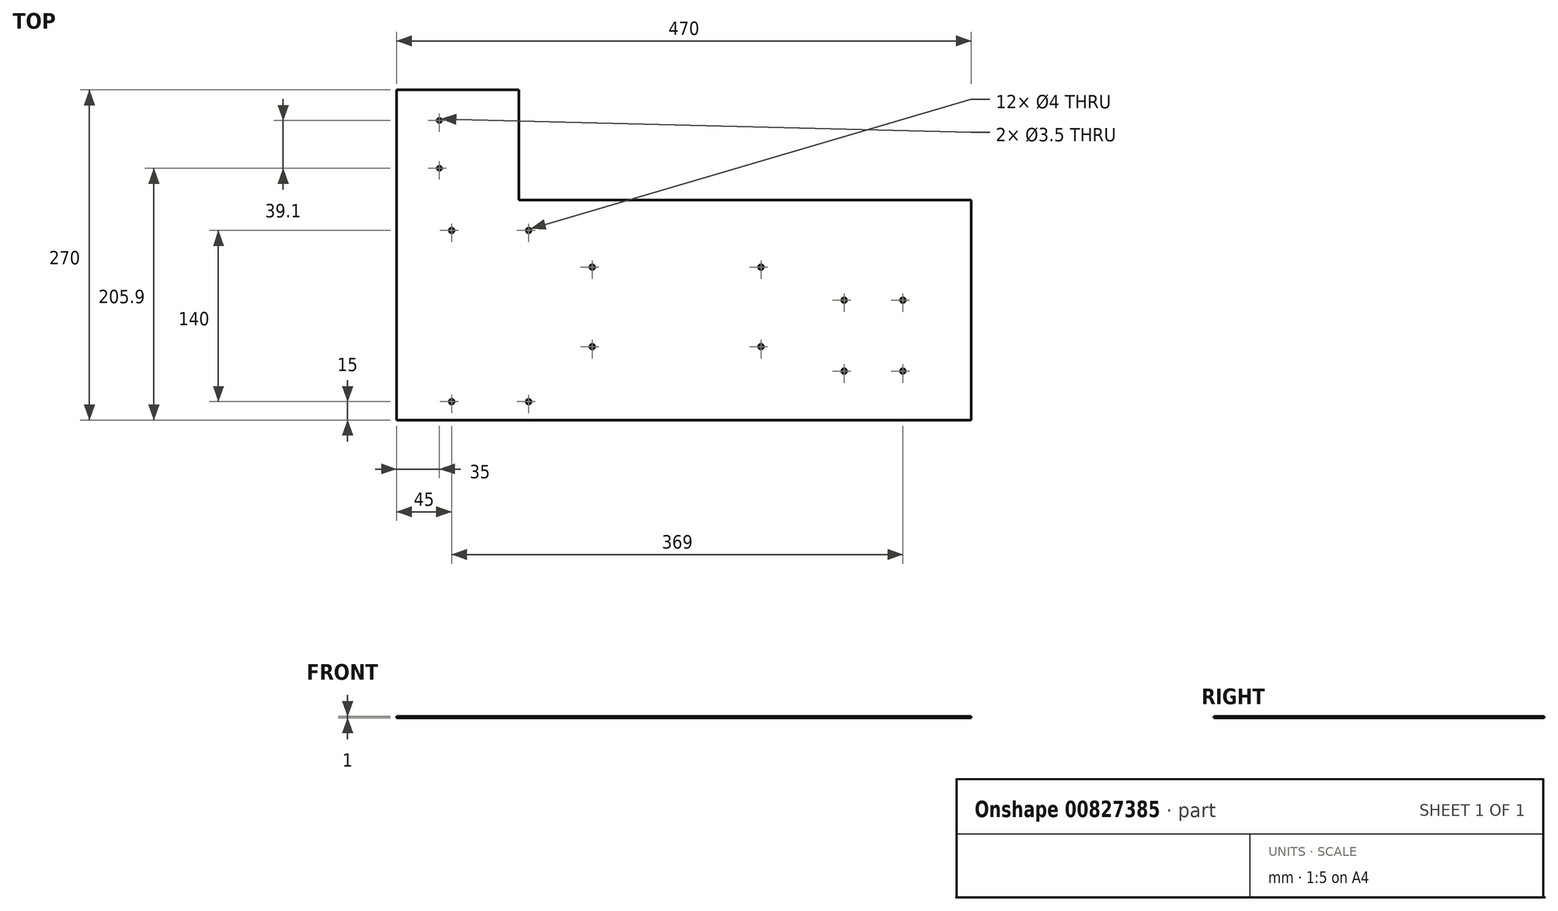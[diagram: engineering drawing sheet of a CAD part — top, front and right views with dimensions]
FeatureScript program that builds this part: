
annotation { "Feature Type Name" : "Feature", "Feature Type Description" : "" }
export const myFeature = defineFeature(function(context is Context, id is Id, definition is map)
    precondition{}
    {
        {
            var Q0;
            Q0=qCreatedBy(makeId("Top.planeOp"),FACE);
            var sketch = newSketch(context, id + "F0", { "sketchPlane" : qUnion([Q0])});
            skLineSegment(sketch, "E0.bottom", {"start": v(-235, 90) * mm, "end": v(-135, 90) * mm, "construction": true});
            skLineSegment(sketch, "E0.top", {"start": v(-235, -90) * mm, "end": v(235, -90) * mm});
            skLineSegment(sketch, "E0.left", {"start": v(-235, 90) * mm, "end": v(-235, -90) * mm});
            skLineSegment(sketch, "E0.right", {"start": v(235, 90) * mm, "end": v(235, -90) * mm});
            skPoint(sketch, "E0.middle", {"position": v(0, 0) * mm});
            skLineSegment(sketch, "E1", {"start": v(-135, 90) * mm, "end": v(-135, 180) * mm});
            skLineSegment(sketch, "E2", {"start": v(-135, 180) * mm, "end": v(-235, 180) * mm});
            skLineSegment(sketch, "E3", {"start": v(-235, 180) * mm, "end": v(-235, 90) * mm});
            skLineSegment(sketch, "E4", {"start": v(-135, 90) * mm, "end": v(235, 90) * mm});
            skSolve(sketch);
        }
        {
            var Q0;
            Q0 = qSketchRegion(id + "F0", true);
            extrude(context, id + "F1", {"entities" : qUnion([Q0]), "depth" : 1 * mm, "offsetDistance" : 25 * mm});
        }
        {
            var Q0;
            Q0=makeQuery(id+"F1.opExtrude","CAP_FACE",FACE,{"disambiguationData":[OSD([sQuery(id+"F0.wireOp",EDGE,"E0.bottom"),sQuery(id+"F0.wireOp",EDGE,"E0.top"),sQuery(id+"F0.wireOp",EDGE,"E0.left"),sQuery(id+"F0.wireOp",EDGE,"E0.right")])],"isStart":false});
            var sketch = newSketch(context, id + "F2", { "sketchPlane" : qUnion([Q0])});
            skLineSegment(sketch, "E5", {"start": v(-419.49, -5) * mm, "end": v(102.49, -5) * mm, "construction": true});
            skLineSegment(sketch, "E6", {"start": v(-158.5, -99.39) * mm, "end": v(-158.5, -5) * mm, "construction": true});
            skPoint(sketch, "E7", {"position": v(-190, 65) * mm});
            skPoint(sketch, "E8.MirrorP", {"position": v(-127, 65) * mm});
            skPoint(sketch, "E9.MirrorP", {"position": v(-127, -75) * mm});
            skPoint(sketch, "E10.MirrorP", {"position": v(-190, -75) * mm});
            skLineSegment(sketch, "E11.bottom", {"start": v(-220, 70) * mm, "end": v(-122, 70) * mm, "construction": true});
            skLineSegment(sketch, "E11.top", {"start": v(-220, -80) * mm, "end": v(-122, -80) * mm, "construction": true});
            skLineSegment(sketch, "E11.left", {"start": v(-220, 70) * mm, "end": v(-220, -80) * mm, "construction": true});
            skLineSegment(sketch, "E11.right", {"start": v(-122, 70) * mm, "end": v(-122, -80) * mm, "construction": true});
            skCircle(sketch, "E12", {"center": v(-127, 65) * mm, "radius": 2 * mm});
            skCircle(sketch, "E13", {"center": v(-190, 65) * mm, "radius": 2 * mm});
            skCircle(sketch, "E14", {"center": v(-127, -75) * mm, "radius": 2 * mm});
            skCircle(sketch, "E15", {"center": v(-190, -75) * mm, "radius": 2 * mm});
            skSolve(sketch);
        }
        {
            var Q0;
            Q0 = qSketchRegion(id + "F2", true);
            extrude(context, id + "F3", {"entities" : qUnion([Q0]), "operationType" : NewBodyOperationType.REMOVE, "endBound" : BoundingType.UP_TO_NEXT, "oppositeDirection" : true, "depth" : 25 * mm, "offsetDistance" : 25 * mm});
        }
        {
            var Q0;
            Q0=makeQuery(id+"F1.opExtrude","CAP_FACE",FACE,{"disambiguationData":[OSD([sQuery(id+"F0.wireOp",EDGE,"E0.bottom"),sQuery(id+"F0.wireOp",EDGE,"E0.top"),sQuery(id+"F0.wireOp",EDGE,"E0.left"),sQuery(id+"F0.wireOp",EDGE,"E0.right")])],"isStart":false});
            var sketch = newSketch(context, id + "F4", { "sketchPlane" : qUnion([Q0])});
            skLineSegment(sketch, "E16", {"start": v(-23.92, 2.5) * mm, "end": v(11.92, 2.5) * mm, "construction": true});
            skLineSegment(sketch, "E17", {"start": v(-6, 2.5) * mm, "end": v(-6, -6.55) * mm, "construction": true});
            skCircle(sketch, "E18", {"center": v(-75, 35) * mm, "radius": 2 * mm});
            skCircle(sketch, "E19.MirrorC", {"center": v(63, 35) * mm, "radius": 2 * mm});
            skCircle(sketch, "E20.MirrorC", {"center": v(-75, -30) * mm, "radius": 2 * mm});
            skCircle(sketch, "E21.MirrorC", {"center": v(63, -30) * mm, "radius": 2 * mm});
            skLineSegment(sketch, "E22.bottom", {"start": v(-81, 40.5) * mm, "end": v(69, 40.5) * mm, "construction": true});
            skLineSegment(sketch, "E22.top", {"start": v(-81, -39.5) * mm, "end": v(69, -39.5) * mm, "construction": true});
            skLineSegment(sketch, "E22.left", {"start": v(-81, 40.5) * mm, "end": v(-81, -39.5) * mm, "construction": true});
            skLineSegment(sketch, "E22.right", {"start": v(69, 40.5) * mm, "end": v(69, -39.5) * mm, "construction": true});
            skSolve(sketch);
        }
        {
            var Q0;
            Q0 = qSketchRegion(id + "F4", true);
            extrude(context, id + "F5", {"entities" : qUnion([Q0]), "operationType" : NewBodyOperationType.REMOVE, "oppositeDirection" : true, "depth" : 25 * mm, "offsetDistance" : 25 * mm});
        }
        {
            var Q0;
            Q0=makeQuery(id+"F1.opExtrude","CAP_FACE",FACE,{"disambiguationData":[OSD([sQuery(id+"F0.wireOp",EDGE,"E0.top"),sQuery(id+"F0.wireOp",EDGE,"E0.left"),sQuery(id+"F0.wireOp",EDGE,"E0.right"),sQuery(id+"F0.wireOp",EDGE,"E1"),sQuery(id+"F0.wireOp",EDGE,"E2"),sQuery(id+"F0.wireOp",EDGE,"E3"),sQuery(id+"F0.wireOp",EDGE,"E4")])],"isStart":false});
            var sketch = newSketch(context, id + "F6", { "sketchPlane" : qUnion([Q0])});
            skLineSegment(sketch, "E23.bottom", {"start": v(-230, 175) * mm, "end": v(-179, 175) * mm, "construction": true});
            skLineSegment(sketch, "E23.top", {"start": v(-230, 113) * mm, "end": v(-179, 113) * mm, "construction": true});
            skLineSegment(sketch, "E23.left", {"start": v(-230, 175) * mm, "end": v(-230, 113) * mm, "construction": true});
            skLineSegment(sketch, "E23.right", {"start": v(-179, 175) * mm, "end": v(-179, 113) * mm, "construction": true});
            skLineSegment(sketch, "E24", {"start": v(155, 34.32) * mm, "end": v(155, -49.14) * mm, "construction": true});
            skLineSegment(sketch, "E25", {"start": v(117.9, -21) * mm, "end": v(155, -21) * mm, "construction": true});
            skCircle(sketch, "E26", {"center": v(131, 8) * mm, "radius": 2 * mm});
            skCircle(sketch, "E27.MirrorC", {"center": v(131, -50) * mm, "radius": 2 * mm});
            skCircle(sketch, "E28.MirrorC", {"center": v(179, 8) * mm, "radius": 2 * mm});
            skCircle(sketch, "E29.MirrorC", {"center": v(179, -50) * mm, "radius": 2 * mm});
            skLineSegment(sketch, "E30.bottom", {"start": v(126.5, 33) * mm, "end": v(183.5, 33) * mm, "construction": true});
            skLineSegment(sketch, "E30.top", {"start": v(126.5, -55) * mm, "end": v(183.5, -55) * mm, "construction": true});
            skLineSegment(sketch, "E30.left", {"start": v(126.5, 33) * mm, "end": v(126.5, -55) * mm, "construction": true});
            skLineSegment(sketch, "E30.right", {"start": v(183.5, 33) * mm, "end": v(183.5, -55) * mm, "construction": true});
            skSolve(sketch);
        }
        {
            var Q0;
            Q0 = qSketchRegion(id + "F6", true);
            extrude(context, id + "F7", {"entities" : qUnion([Q0]), "operationType" : NewBodyOperationType.REMOVE, "oppositeDirection" : true, "depth" : 25 * mm, "offsetDistance" : 25 * mm});
        }
        {
            var Q0;
            Q0=makeQuery(id+"F1.opExtrude","CAP_FACE",FACE,{"disambiguationData":[OSD([sQuery(id+"F0.wireOp",EDGE,"E0.top"),sQuery(id+"F0.wireOp",EDGE,"E0.left"),sQuery(id+"F0.wireOp",EDGE,"E0.right"),sQuery(id+"F0.wireOp",EDGE,"E1"),sQuery(id+"F0.wireOp",EDGE,"E2"),sQuery(id+"F0.wireOp",EDGE,"E3"),sQuery(id+"F0.wireOp",EDGE,"E4")])],"isStart":false});
            var sketch = newSketch(context, id + "F8", { "sketchPlane" : qUnion([Q0])});
            skLineSegment(sketch, "E31", {"start": v(-200, 165.4) * mm, "end": v(-200, 97.39) * mm, "construction": true});
            skLineSegment(sketch, "E32", {"start": v(-247.79, 135.45) * mm, "end": v(-200, 135.45) * mm, "construction": true});
            skCircle(sketch, "E33", {"center": v(-200, 155) * mm, "radius": 1.75 * mm});
            skCircle(sketch, "E34.MirrorC", {"center": v(-200, 115.9) * mm, "radius": 1.75 * mm});
            skLineSegment(sketch, "E35.bottom", {"start": v(-225.5, 169.65) * mm, "end": v(-174.5, 169.65) * mm, "construction": true});
            skLineSegment(sketch, "E35.top", {"start": v(-225.5, 107.15) * mm, "end": v(-174.5, 107.15) * mm, "construction": true});
            skLineSegment(sketch, "E35.left", {"start": v(-225.5, 169.65) * mm, "end": v(-225.5, 107.15) * mm, "construction": true});
            skLineSegment(sketch, "E35.right", {"start": v(-174.5, 169.65) * mm, "end": v(-174.5, 107.15) * mm, "construction": true});
            skLineSegment(sketch, "E36.bottom", {"start": v(-220, 107.15) * mm, "end": v(-180, 107.15) * mm, "construction": true});
            skLineSegment(sketch, "E36.top", {"start": v(-220, 95.15) * mm, "end": v(-180, 95.15) * mm, "construction": true});
            skLineSegment(sketch, "E36.left", {"start": v(-220, 107.15) * mm, "end": v(-220, 95.15) * mm, "construction": true});
            skLineSegment(sketch, "E36.right", {"start": v(-180, 107.15) * mm, "end": v(-180, 95.15) * mm, "construction": true});
            skSolve(sketch);
        }
        {
            var Q0;
            Q0 = qSketchRegion(id + "F8", true);
            extrude(context, id + "F9", {"entities" : qUnion([Q0]), "operationType" : NewBodyOperationType.REMOVE, "oppositeDirection" : true, "depth" : 25 * mm, "offsetDistance" : 25 * mm});
        }
    });
